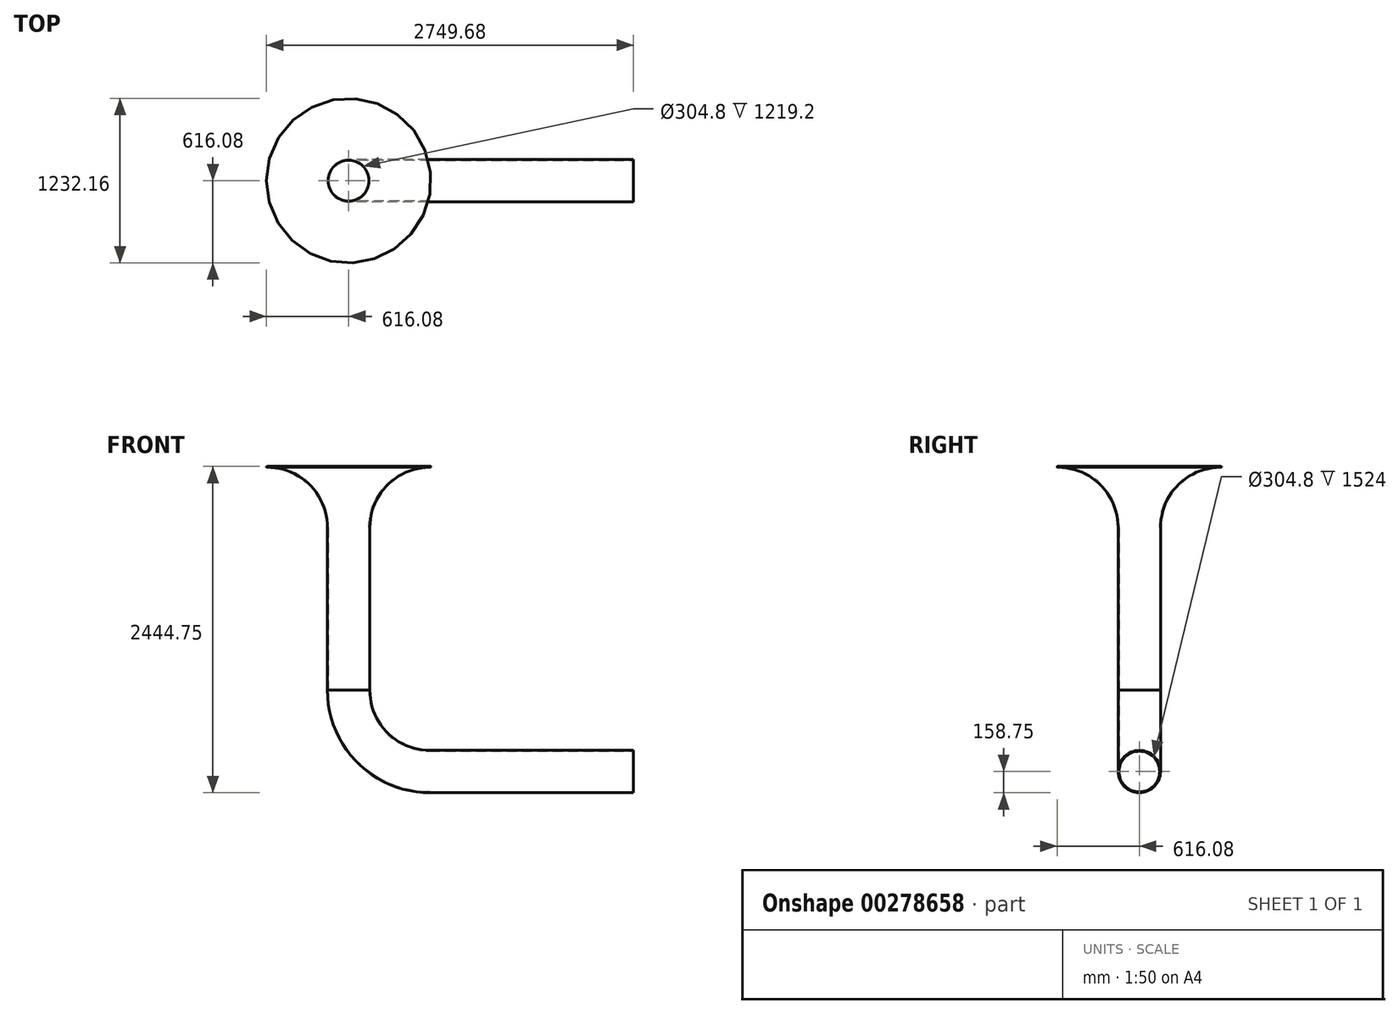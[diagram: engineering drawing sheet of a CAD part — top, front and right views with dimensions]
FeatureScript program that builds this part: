
annotation { "Feature Type Name" : "Feature", "Feature Type Description" : "" }
export const myFeature = defineFeature(function(context is Context, id is Id, definition is map)
    precondition{}
    {
        {
            var Q0;
            Q0=qCreatedBy(makeId("Front.planeOp"),FACE);
            var sketch = newSketch(context, id + "F0", { "sketchPlane" : qUnion([Q0])});
            skLineSegment(sketch, "E0", {"start": v(0, 609.6) * mm, "end": v(0, 1828.8) * mm});
            skLineSegment(sketch, "E1", {"start": v(609.6, 0) * mm, "end": v(2133.6, 0) * mm});
            skPoint(sketch, "E2.visualSharp", {"position": v(0, 0) * mm});
            skArc(sketch, "E2.filletArc", {"start": v(0, 609.6) * mm, "mid": v(178.55, 178.55) * mm, "end": v(609.6, 0) * mm});
            skLineSegment(sketch, "E3", {"start": v(0, 1828.8) * mm, "end": v(0, 2286) * mm});
            skLineSegment(sketch, "E4", {"start": v(2133.6, 0) * mm, "end": v(2743.2, 0) * mm});
            skLineSegment(sketch, "E5", {"start": v(2743.2, 0) * mm, "end": v(3352.8, 0) * mm});
            skSolve(sketch);
        }
        {
            var Q0;
            Q0=qCreatedBy(makeId("Front.planeOp"),FACE);
            var sketch = newSketch(context, id + "F1", { "sketchPlane" : qUnion([Q0])});
            skLineSegment(sketch, "E6.0", {"start": v(152.4, 609.6) * mm, "end": v(152.4, 1828.8) * mm});
            skArc(sketch, "E7", {"start": v(152.4, 1828.8) * mm, "mid": v(287.5, 2153.27) * mm, "end": v(612.93, 2285.99) * mm});
            skArc(sketch, "E8.0", {"start": v(158.75, 1828.8) * mm, "mid": v(291.97, 2148.76) * mm, "end": v(612.89, 2279.64) * mm});
            skLineSegment(sketch, "E8.1", {"start": v(158.75, 609.6) * mm, "end": v(158.75, 1828.8) * mm});
            skArc(sketch, "E9", {"start": v(612.93, 2285.99) * mm, "mid": v(616.08, 2282.79) * mm, "end": v(612.89, 2279.64) * mm});
            skLineSegment(sketch, "E10", {"start": v(152.4, 609.6) * mm, "end": v(158.75, 609.6) * mm});
            skSolve(sketch);
        }
        {
            var Q0;
            Q0=qCreatedBy(makeId("Top.planeOp"),FACE);
            cPlane(context, id + "F2", {"entities" : qUnion([Q0]), "cplaneType" : CPlaneType.OFFSET, "offset" : 609.6 * mm, "width" : 152.4 * mm, "height" : 152.4 * mm});
        }
        {
            var Q0;
            Q0=qCreatedBy(id+"F2.planeOp",FACE);
            var sketch = newSketch(context, id + "F3", { "sketchPlane" : qUnion([Q0])});
            skCircle(sketch, "E11", {"center": v(0, 0) * mm, "radius": 152.4 * mm});
            skCircle(sketch, "E12.0", {"center": v(0, 0) * mm, "radius": 158.75 * mm});
            skSolve(sketch);
        }
        {
            var Q0;
            Q0=makeQuery(id+"F3.imprint","IMPRINT",FACE,{"disambiguationData":[TD([[makeQuery(id+"F3.imprint","IMPRINT",EDGE,{"derivedFrom":sQuery(id+"F3.wireOp",EDGE,"E11")}),-1.0]])]});
            var Q1;
            Q1=sQuery(id+"F0.wireOp",EDGE,"E2.filletArc");
            var Q2;
            Q2=sQuery(id+"F0.wireOp",EDGE,"E1");
            sweep(context, id + "F4", {"profiles" : qUnion([Q0]), "path" : qUnion([Q1, Q2])});
        }
        {
            var Q0;
            Q0=makeQuery(id+"F1.imprint","IMPRINT",FACE,{"disambiguationData":[TD([[makeQuery(id+"F1.imprint","IMPRINT",EDGE,{"derivedFrom":sQuery(id+"F1.wireOp",EDGE,"E6.0")}),-1.0]])]});
            var Q1;
            Q1=sQuery(id+"F0.wireOp",EDGE,"E3");
            revolve(context, id + "F5", {"entities" : qUnion([Q0]), "axis" : qUnion([Q1]), "revolveType" : RevolveType.FULL});
        }
    });
